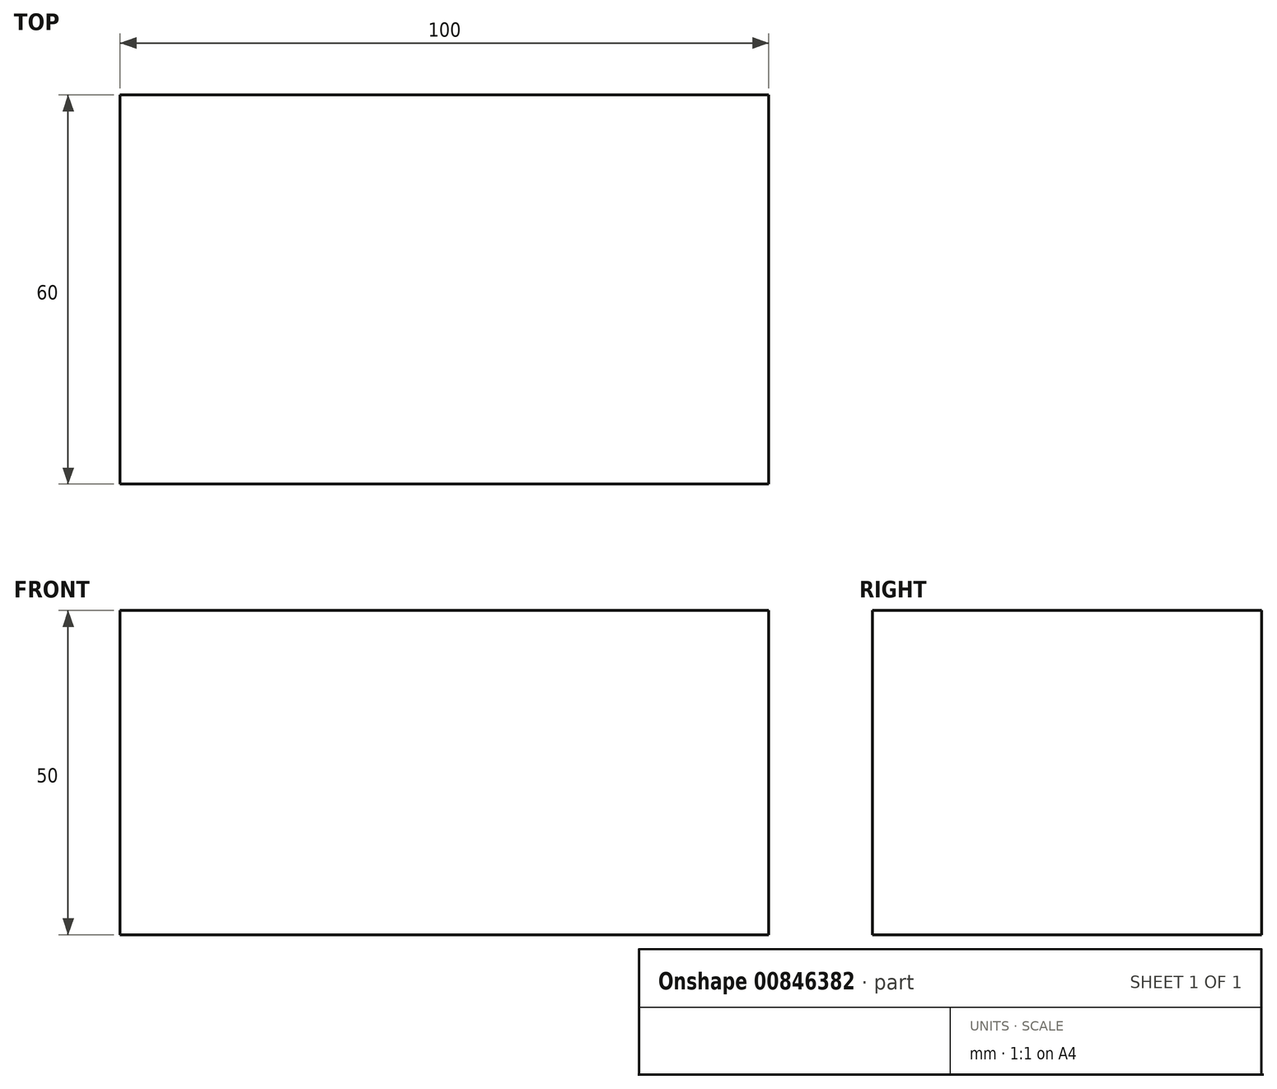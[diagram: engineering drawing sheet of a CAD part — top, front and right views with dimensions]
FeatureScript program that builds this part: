
annotation { "Feature Type Name" : "Feature", "Feature Type Description" : "" }
export const myFeature = defineFeature(function(context is Context, id is Id, definition is map)
    precondition{}
    {
        {
            var Q0;
            Q0=qCreatedBy(makeId("Top.planeOp"),FACE);
            var sketch = newSketch(context, id + "F0", { "sketchPlane" : qUnion([Q0])});
            skLineSegment(sketch, "E0.bottom", {"start": v(50, -30) * mm, "end": v(-50, -30) * mm});
            skLineSegment(sketch, "E0.top", {"start": v(50, 30) * mm, "end": v(-50, 30) * mm});
            skLineSegment(sketch, "E0.left", {"start": v(50, -30) * mm, "end": v(50, 30) * mm});
            skLineSegment(sketch, "E0.right", {"start": v(-50, -30) * mm, "end": v(-50, 30) * mm});
            skPoint(sketch, "E0.middle", {"position": v(0, 0) * mm});
            skSolve(sketch);
        }
        {
            var Q0;
            Q0=makeQuery(id+"F0.imprint","IMPRINT",FACE,{"disambiguationData":[TD([[makeQuery(id+"F0.imprint","IMPRINT",EDGE,{"derivedFrom":sQuery(id+"F0.wireOp",EDGE,"E0.bottom")}),-1.0]])]});
            extrude(context, id + "F1", {"entities" : qUnion([Q0]), "depth" : 50 * mm, "offsetDistance" : 25 * mm});
        }
    });
